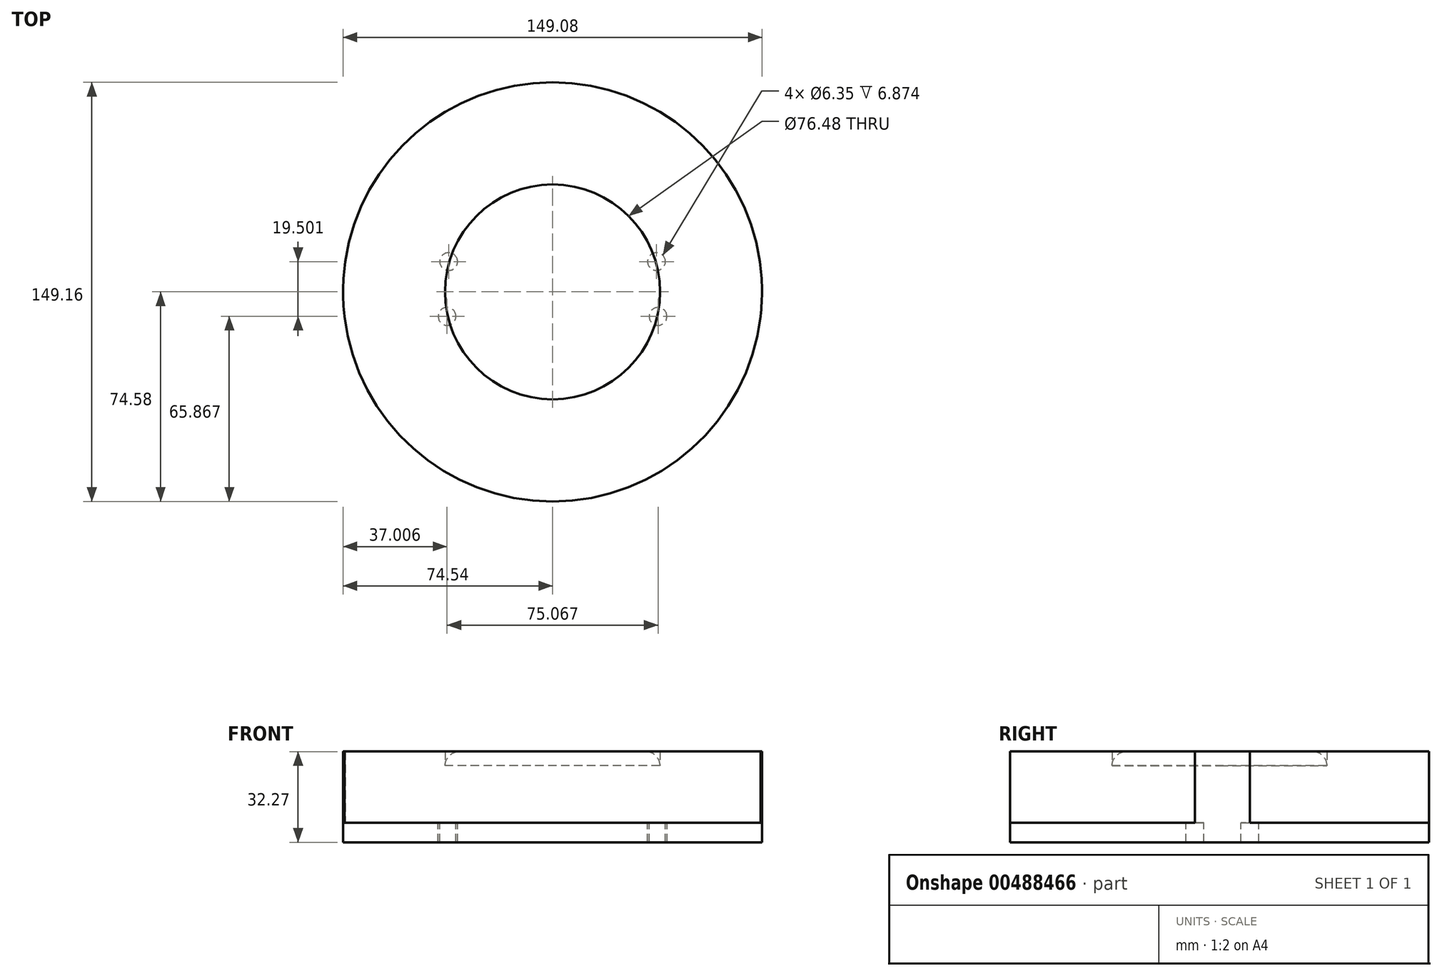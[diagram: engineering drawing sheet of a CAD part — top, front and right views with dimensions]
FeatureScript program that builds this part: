
annotation { "Feature Type Name" : "Feature", "Feature Type Description" : "" }
export const myFeature = defineFeature(function(context is Context, id is Id, definition is map)
    precondition{}
    {
        {
            var Q0;
            Q0=qCreatedBy(makeId("Top.planeOp"),FACE);
            var sketch = newSketch(context, id + "F0", { "sketchPlane" : qUnion([Q0])});
            skCircle(sketch, "E0", {"center": v(0, 0) * mm, "radius": 74.54 * mm});
            skSolve(sketch);
        }
        {
            var Q0;
            Q0 = qSketchRegion(id + "F0", true);
            extrude(context, id + "F1", {"entities" : qUnion([Q0]), "depth" : 6.87 * mm});
        }
        {
            var Q0;
            Q0=makeQuery(id+"F1.opExtrude","CAP_FACE",FACE,{"disambiguationData":[OSD([sQuery(id+"F0.wireOp",EDGE,"E0")])],"isStart":false});
            var sketch = newSketch(context, id + "F2", { "sketchPlane" : qUnion([Q0])});
            skArc(sketch, "E1", {"start": v(-74.07, -8.71) * mm, "mid": v(0, -74.58) * mm, "end": v(74.07, -8.71) * mm});
            skArc(sketch, "E2", {"start": v(-37.53, -8.71) * mm, "mid": v(0, -38.53) * mm, "end": v(37.53, -8.71) * mm});
            skLineSegment(sketch, "E3.bottom", {"start": v(-73.8, 10.79) * mm, "end": v(-37, 10.79) * mm});
            skLineSegment(sketch, "E3.top", {"start": v(-74.07, -8.71) * mm, "end": v(-37.53, -8.71) * mm});
            skArc(sketch, "E4.trimOffspring", {"start": v(37, 10.79) * mm, "mid": v(0, 38.53) * mm, "end": v(-37, 10.79) * mm});
            skArc(sketch, "E5.trimOffspring", {"start": v(73.8, 10.79) * mm, "mid": v(0, 74.58) * mm, "end": v(-73.8, 10.79) * mm});
            skLineSegment(sketch, "E6.trimOffspring", {"start": v(37, 10.79) * mm, "end": v(73.8, 10.79) * mm});
            skLineSegment(sketch, "E7.trimOffspring", {"start": v(37.53, -8.71) * mm, "end": v(74.07, -8.71) * mm});
            skCircle(sketch, "E8", {"center": v(0, 0) * mm, "radius": 38.24 * mm});
            skSolve(sketch);
        }
        {
            var Q0;
            Q0 = qSketchRegion(id + "F2", true);
            extrude(context, id + "F3", {"entities" : qUnion([Q0]), "operationType" : NewBodyOperationType.ADD, "depth" : 25.4 * mm});
        }
        {
            var Q0;
            Q0=makeQuery(id+"F3.opExtrude","CAP_FACE",FACE,{"disambiguationData":[OSD([sQuery(id+"F2.wireOp",EDGE,"E8")])],"isStart":false});
            fillet(context, id + "F4", {"entities" : qUnion([Q0]), "radius" : 5.08 * mm, "tangentPropagation" : true, "allowEdgeOverflow" : false});
        }
        {
            var Q0;
            Q0=makeQuery(id+"F1.opExtrude","CAP_FACE",FACE,{"disambiguationData":[OSD([sQuery(id+"F0.wireOp",EDGE,"E0")])],"isStart":false});
            extrude(context, id + "F5", {"entities" : qUnion([Q0]), "operationType" : NewBodyOperationType.ADD, "depth" : 25.4 * mm});
        }
        {
            var Q0;
            Q0=sQuery(id+"F2.wireOp",VERTEX,"E4.trimOffspring.end");
            var Q1;
            Q1=makeQuery(id+"F1.opExtrude","SWEPT_BODY",BODY,{"disambiguationData":[OSD([sQuery(id+"F0.wireOp",EDGE,"E0")])]});
            hole(context, id + "F6", {"style" : HoleStyle.SIMPLE, "endStyle" : HoleEndStyle.BLIND, "holeDiameter" : 6.35 * mm, "holeDepth" : 2514.6 * mm, "isTappedThrough" : true, "tappedDepth" : 12.7 * mm, "tapClearance" : 3, "locations" : qUnion([Q0]), "scope" : qUnion([Q1])});
        }
        {
            var Q0;
            Q0=sQuery(id+"F2.wireOp",VERTEX,"E3.top.end");
            var Q1;
            Q1=makeQuery(id+"F1.opExtrude","SWEPT_BODY",BODY,{"disambiguationData":[OSD([sQuery(id+"F0.wireOp",EDGE,"E0")])]});
            hole(context, id + "F7", {"style" : HoleStyle.SIMPLE, "endStyle" : HoleEndStyle.BLIND, "holeDiameter" : 6.35 * mm, "holeDepth" : 2514.6 * mm, "isTappedThrough" : true, "tappedDepth" : 12.7 * mm, "tapClearance" : 3, "locations" : qUnion([Q0]), "scope" : qUnion([Q1])});
        }
        {
            var Q0;
            Q0=sQuery(id+"F2.wireOp",VERTEX,"E6.trimOffspring.start");
            var Q1;
            Q1=makeQuery(id+"F1.opExtrude","SWEPT_BODY",BODY,{"disambiguationData":[OSD([sQuery(id+"F0.wireOp",EDGE,"E0")])]});
            hole(context, id + "F8", {"style" : HoleStyle.SIMPLE, "endStyle" : HoleEndStyle.BLIND, "holeDiameter" : 6.35 * mm, "holeDepth" : 12.7 * mm, "isTappedThrough" : true, "tappedDepth" : 12.7 * mm, "tapClearance" : 3, "locations" : qUnion([Q0]), "scope" : qUnion([Q1])});
        }
        {
            var Q0;
            Q0=sQuery(id+"F2.wireOp",VERTEX,"E2.end");
            var Q1;
            Q1=makeQuery(id+"F1.opExtrude","SWEPT_BODY",BODY,{"disambiguationData":[OSD([sQuery(id+"F0.wireOp",EDGE,"E0")])]});
            hole(context, id + "F9", {"style" : HoleStyle.SIMPLE, "endStyle" : HoleEndStyle.BLIND, "holeDiameter" : 6.35 * mm, "holeDepth" : 2514.6 * mm, "isTappedThrough" : true, "tappedDepth" : 12.7 * mm, "tapClearance" : 3, "locations" : qUnion([Q0]), "scope" : qUnion([Q1])});
        }
    });
